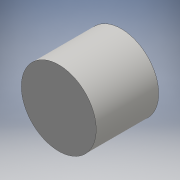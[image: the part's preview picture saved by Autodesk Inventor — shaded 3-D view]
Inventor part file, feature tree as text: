
AUTODESK INVENTOR PART (.ipt)
format: ipt  version: 2016 (Build 200138000, 138)  size: 87,040 bytes
history: native  units: mm
features: extrude x1, sketch x1
ambient origin geometry x8: Origin, YZ Plane, XZ Plane, XY Plane, X Axis, Y Axis, Z Axis, Center Point
bodies: Solid1 (feature_tree)
feature tree (2):
  extrude  "Extrusion1"  Depth=10.0mm TaperAngle=0.0deg
  sketch  "Sketch1"  dims[d0=12.0mm d1=10.0mm d2=0.0mm]
